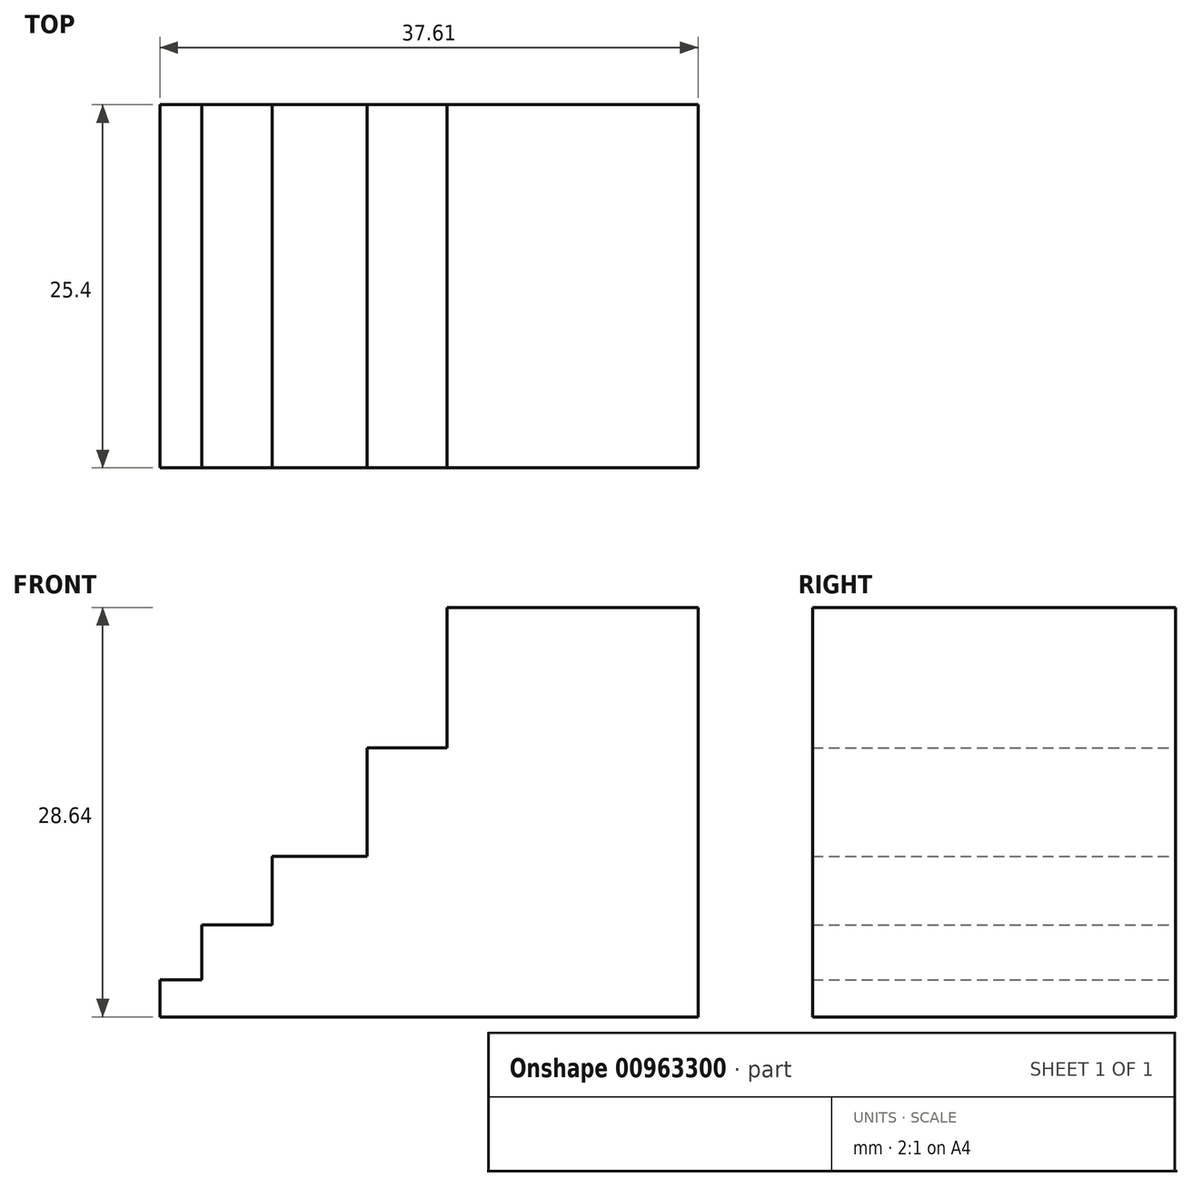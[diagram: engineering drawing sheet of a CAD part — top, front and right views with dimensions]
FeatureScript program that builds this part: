
annotation { "Feature Type Name" : "Feature", "Feature Type Description" : "" }
export const myFeature = defineFeature(function(context is Context, id is Id, definition is map)
    precondition{}
    {
        {
            var Q0;
            Q0=qCreatedBy(makeId("Front.planeOp"),FACE);
            var sketch = newSketch(context, id + "F0", { "sketchPlane" : qUnion([Q0])});
            skLineSegment(sketch, "E0", {"start": v(-26.58, 0) * mm, "end": v(-26.58, 2.6) * mm});
            skLineSegment(sketch, "E1", {"start": v(-26.58, 2.6) * mm, "end": v(11.03, 2.6) * mm});
            skLineSegment(sketch, "E2", {"start": v(21.13, 0) * mm, "end": v(-26.58, 0) * mm});
            skLineSegment(sketch, "E3", {"start": v(11.03, 6.45) * mm, "end": v(-23.65, 6.45) * mm});
            skLineSegment(sketch, "E4", {"start": v(-23.65, 6.45) * mm, "end": v(-23.65, 2.6) * mm});
            skLineSegment(sketch, "E5", {"start": v(11.03, 11.23) * mm, "end": v(-18.74, 11.23) * mm});
            skLineSegment(sketch, "E6", {"start": v(-18.74, 11.23) * mm, "end": v(-18.74, 6.45) * mm});
            skLineSegment(sketch, "E7", {"start": v(11.03, 18.8) * mm, "end": v(-12.1, 18.8) * mm});
            skLineSegment(sketch, "E8", {"start": v(-12.1, 18.8) * mm, "end": v(-12.1, 11.23) * mm});
            skLineSegment(sketch, "E9", {"start": v(11.03, 18.8) * mm, "end": v(11.03, 28.64) * mm});
            skLineSegment(sketch, "E10", {"start": v(11.03, 28.64) * mm, "end": v(-6.5, 28.64) * mm});
            skLineSegment(sketch, "E11", {"start": v(-6.5, 28.64) * mm, "end": v(-6.5, 18.8) * mm});
            skLineSegment(sketch, "E12", {"start": v(11.03, 18.8) * mm, "end": v(11.03, 0) * mm});
            skLineSegment(sketch, "E13", {"start": v(11.03, 0) * mm, "end": v(11.03, 11.23) * mm});
            skLineSegment(sketch, "E14", {"start": v(11.03, 11.23) * mm, "end": v(11.03, 6.45) * mm});
            skLineSegment(sketch, "E15", {"start": v(11.03, 6.45) * mm, "end": v(11.03, 2.6) * mm});
            skPoint(sketch, "E16.end.orphan", {"position": v(17.01, 11.23) * mm});
            skPoint(sketch, "E17.end.orphan", {"position": v(18.6, 6.45) * mm});
            skSolve(sketch);
        }
        {
            var Q0;
            Q0 = qSketchRegion(id + "F0", true);
            extrude(context, id + "F1", {"entities" : qUnion([Q0]), "depth" : 25.4 * mm, "offsetDistance" : 25.4 * mm});
        }
    });
